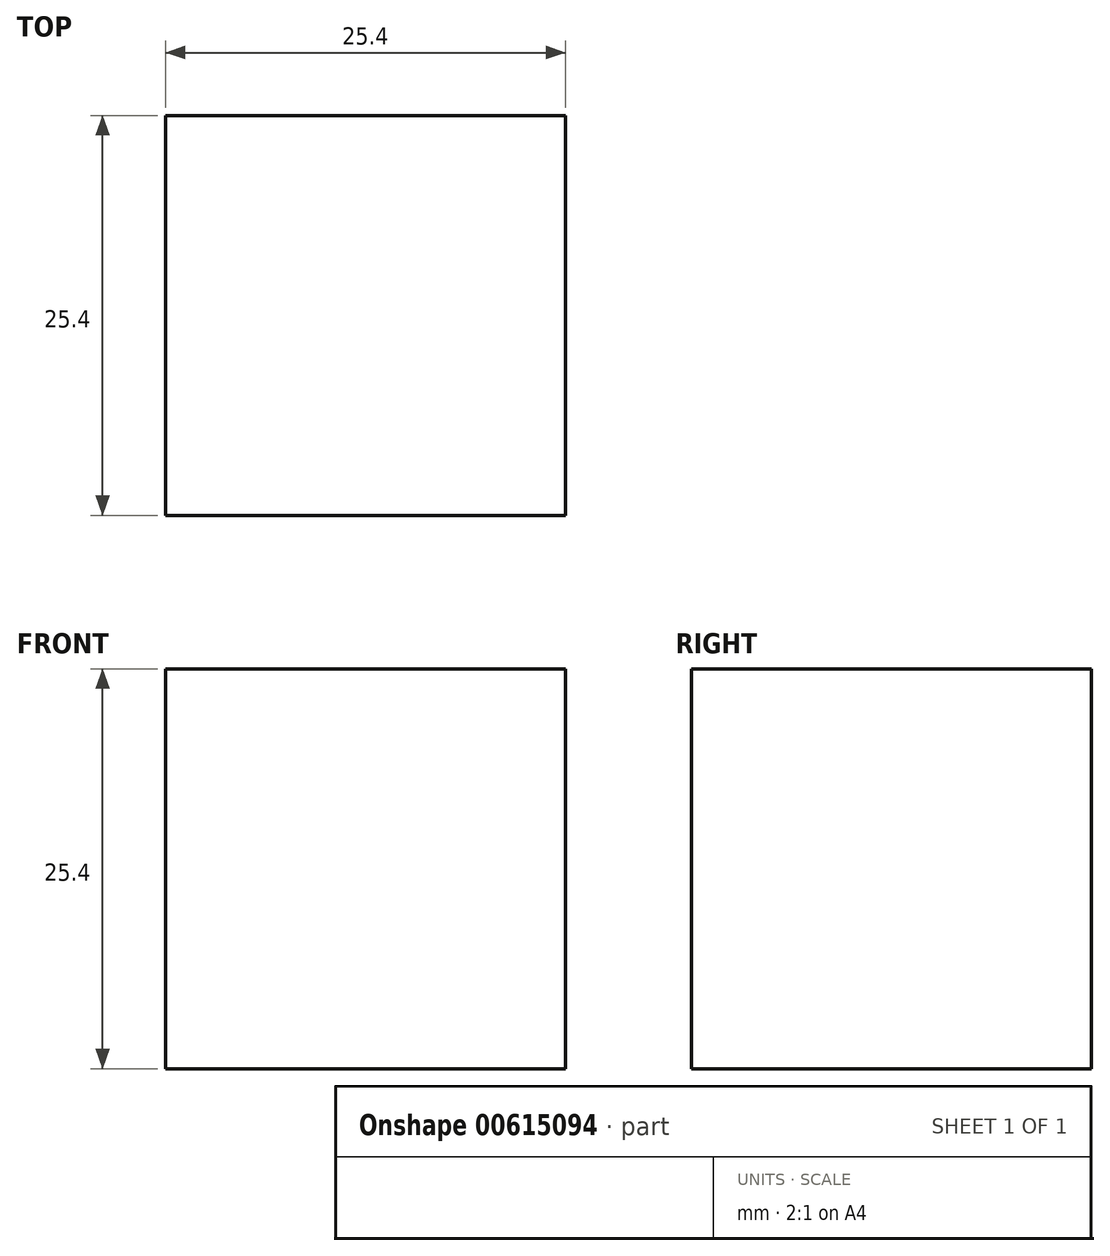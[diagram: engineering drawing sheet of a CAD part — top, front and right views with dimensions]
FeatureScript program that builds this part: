
annotation { "Feature Type Name" : "Feature", "Feature Type Description" : "" }
export const myFeature = defineFeature(function(context is Context, id is Id, definition is map)
    precondition{}
    {
        {
            var Q0;
            Q0=qCreatedBy(makeId("Top.planeOp"),FACE);
            var sketch = newSketch(context, id + "F0", { "sketchPlane" : qUnion([Q0])});
            skLineSegment(sketch, "E0.bottom", {"start": v(12.7, -12.7) * mm, "end": v(-12.7, -12.7) * mm});
            skLineSegment(sketch, "E0.top", {"start": v(12.7, 12.7) * mm, "end": v(-12.7, 12.7) * mm});
            skLineSegment(sketch, "E0.left", {"start": v(12.7, -12.7) * mm, "end": v(12.7, 12.7) * mm});
            skLineSegment(sketch, "E0.right", {"start": v(-12.7, -12.7) * mm, "end": v(-12.7, 12.7) * mm});
            skPoint(sketch, "E0.middle", {"position": v(0, 0) * mm});
            skSolve(sketch);
        }
        {
            var Q0;
            Q0=makeQuery(id+"F0.imprint","IMPRINT",FACE,{"disambiguationData":[TD([[makeQuery(id+"F0.imprint","IMPRINT",EDGE,{"derivedFrom":sQuery(id+"F0.wireOp",EDGE,"E0.bottom")}),-1.0]])]});
            extrude(context, id + "F1", {"entities" : qUnion([Q0]), "depth" : 25.4 * mm, "offsetDistance" : 25.4 * mm});
        }
    });
